# Revit family: TILE T
name_source: partatom
category: Осветительные приборы
revit_build: Autodesk Revit 2016 (Build: 20150714_1515(x64)
units: mm (PartAtom-declared; Revit-internal decimal feet)

## family parameters
Источник света = Нет
Общий = Нет
Основа = Грань
При загрузке вырезать с полостями = Нет
Размер круглого соединителя = Использовать диаметр
Тип детали = Нормальный
Точка расчета площади = Нет

## types (1)
- TILE T
    ADSK_Единица измерения = Шт.
    ADSK_Завод-изготовитель = ООО МГК Световые технологии
    ADSK_Классификация нагрузок = Прочее
    ADSK_Количество фаз = 1
    ADSK_Количество фаз числовое = 1
    ADSK_Коэффициент мощности = 0.9
    ADSK_Масса = 0
    ADSK_Наименование = Трековый светодиодный светильник направленного света изготовлен из алюминия, окрашенного матовой краской. Стандартный цвет: WH – белый. В качестве оптического элемента используется линза, стандартный угол – 45 град. Возможны специальные модификации для освещения в супермаркетах со специализированными светодиодами
    ADSK_Напряжение = 230 В
    ADSK_Номинальная мощность = 0 кВт
    ADSK_Полная мощность = 0 кВ·А
    ADSK_Размер_Высота = 118 мм
    ADSK_Размер_Радиус = 30 мм
    ADSK_Ток = 0 А
    ADSK_Энергоэффективность = 0 лм/Вт
    IP Class = IP20
    URL = http://www.ltcompany.com
    Блок аварийного питания = Нет
    Выбор ИС = IES  TILE T : TILE T 33 WH D45 4000K
    Выбор корпуса = верх TILE T
    Выбор основания = низ TILE T
    Группа модели = Светильники
    Да = Нет
    Изготовитель = ООО МГК Световые технологии
    Класс Защиты = I
    Климатическая зона = УХЛ4
    Код по классификатору = D5020200
    Корпус = Черный металл
    Корпус X = 10 мм
    Корпус Y = 0 мм
    Нет = Нет
    Область использования = Гостиницы, Индивидуальные дома, Культурно-развлекательные, Магазины/Бутики, Объекты бытового обслуживания, Объекты общественного питания, Офисы, ТРЦ
    Описание = Трековый светодиодный светильник направленного света изготовлен из алюминия, окрашенного матовой краской. Стандартный цвет: WH – белый. В качестве оптического элемента используется линза, стандартный угол – 45 град. Возможны специальные модификации для освещения в супермаркетах со специализированными светодиодами
    Отметка по умолчанию = 0 мм
    Плафон = Плафон самосвечение
    Полная установленная мощность = 0 кВ·А
    Смещение ИС = 99 мм
    Тип ИС = LED
    Тип ПРА = Драйвер
    Тип продукции = Светильники
    Толщина основания = 80 мм

## geometry (parser evidence)
native form markers: Blend x28
no freeform markers — native parametric forms only
